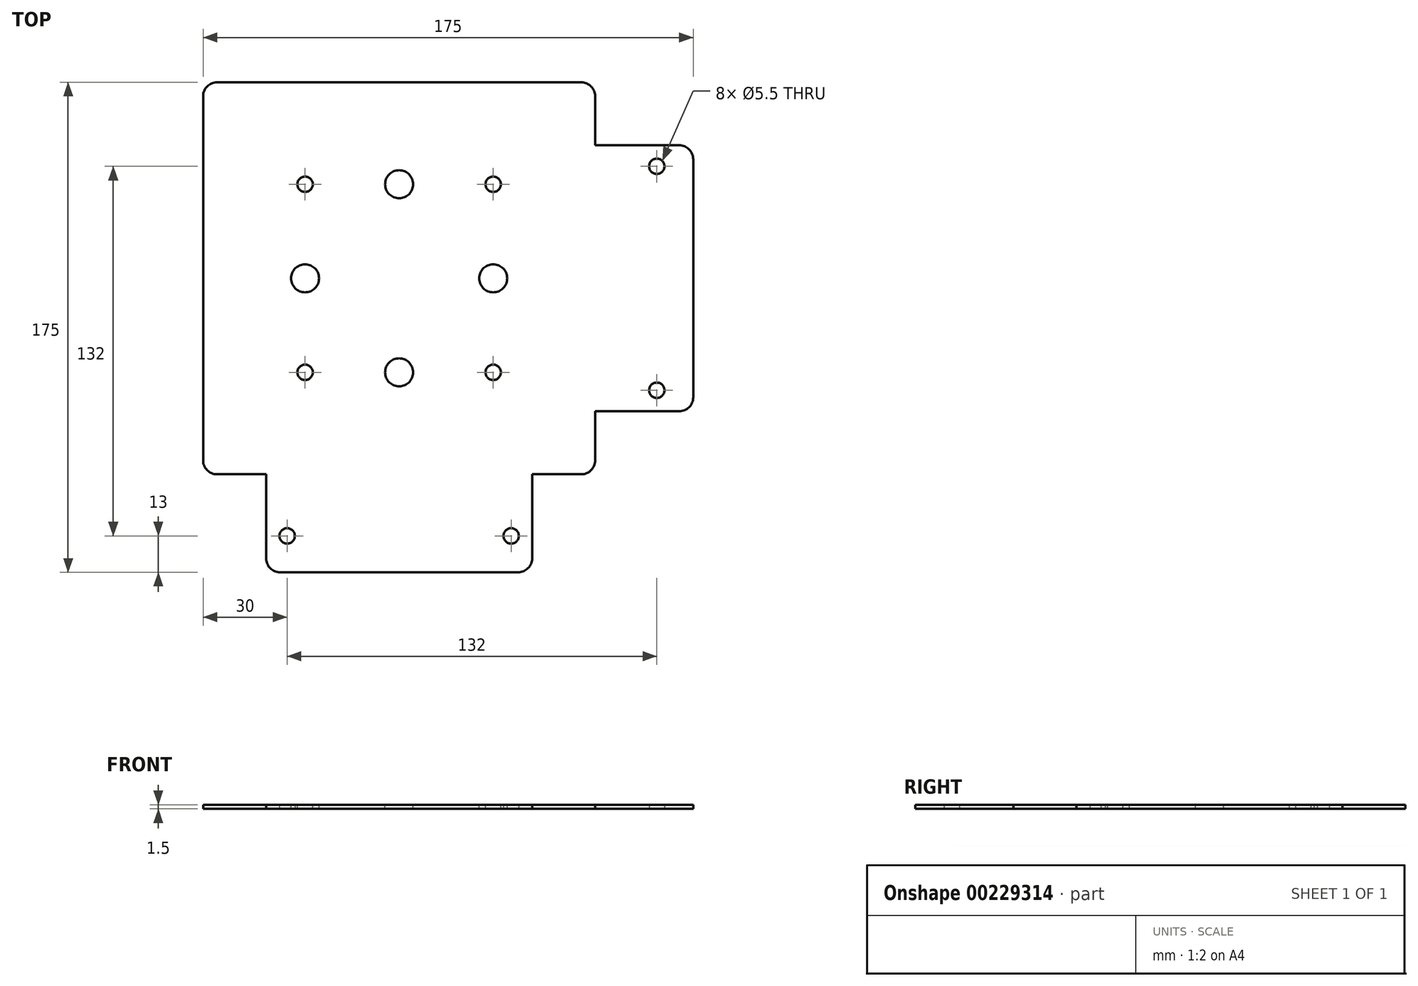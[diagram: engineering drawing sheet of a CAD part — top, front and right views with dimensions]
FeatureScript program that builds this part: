
annotation { "Feature Type Name" : "Feature", "Feature Type Description" : "" }
export const myFeature = defineFeature(function(context is Context, id is Id, definition is map)
    precondition{}
    {
        {
            var Q0;
            Q0=qCreatedBy(makeId("Top.planeOp"),FACE);
            var sketch = newSketch(context, id + "F0", { "sketchPlane" : qUnion([Q0])});
            skLineSegment(sketch, "E0.bottom", {"start": v(-70, 70) * mm, "end": v(70, 70) * mm});
            skLineSegment(sketch, "E0.top", {"start": v(-70, -70) * mm, "end": v(70, -70) * mm});
            skLineSegment(sketch, "E0.left", {"start": v(-70, 70) * mm, "end": v(-70, -70) * mm});
            skLineSegment(sketch, "E0.right", {"start": v(70, 70) * mm, "end": v(70, -70) * mm});
            skPoint(sketch, "E0.middle", {"position": v(0, 0) * mm});
            skLineSegment(sketch, "E1.bottom", {"start": v(-47.5, -70) * mm, "end": v(47.5, -70) * mm});
            skLineSegment(sketch, "E1.top", {"start": v(-47.5, -105) * mm, "end": v(47.5, -105) * mm});
            skLineSegment(sketch, "E1.left", {"start": v(-47.5, -70) * mm, "end": v(-47.5, -105) * mm});
            skLineSegment(sketch, "E1.right", {"start": v(47.5, -70) * mm, "end": v(47.5, -105) * mm});
            skLineSegment(sketch, "E2", {"start": v(70, -70) * mm, "end": v(0, 0) * mm, "construction": true});
            skCircle(sketch, "E3", {"center": v(-40, -92) * mm, "radius": 2.75 * mm});
            skCircle(sketch, "E4", {"center": v(40, -92) * mm, "radius": 2.75 * mm});
            skLineSegment(sketch, "E5.MirrorCS", {"start": v(70, -47.5) * mm, "end": v(105, -47.5) * mm});
            skCircle(sketch, "E6.MirrorC", {"center": v(92, 40) * mm, "radius": 2.75 * mm});
            skCircle(sketch, "E7.MirrorC", {"center": v(92, -40) * mm, "radius": 2.75 * mm});
            skLineSegment(sketch, "E8.MirrorCS", {"start": v(70, 47.5) * mm, "end": v(70, -47.5) * mm});
            skLineSegment(sketch, "E9.MirrorCS", {"start": v(105, 47.5) * mm, "end": v(105, -47.5) * mm});
            skLineSegment(sketch, "E10.MirrorCS", {"start": v(70, 47.5) * mm, "end": v(105, 47.5) * mm});
            skSolve(sketch);
        }
        {
            var Q0;
            Q0 = qSketchRegion(id + "F0", true);
            extrude(context, id + "F1", {"entities" : qUnion([Q0]), "depth" : 1.5 * mm});
        }
        {
            var Q0;
            Q0=makeQuery(id+"F1.opExtrude","CAP_FACE",FACE,{"disambiguationData":[OSD([sQuery(id+"F0.wireOp",EDGE,"E0.bottom"),sQuery(id+"F0.wireOp",EDGE,"E0.top"),sQuery(id+"F0.wireOp",EDGE,"E0.left"),sQuery(id+"F0.wireOp",EDGE,"E0.right")])],"isStart":false});
            var sketch = newSketch(context, id + "F2", { "sketchPlane" : qUnion([Q0])});
            skCircle(sketch, "E11", {"center": v(0, 0) * mm, "radius": 47.5 * mm, "construction": true});
            skCircle(sketch, "E12", {"center": v(-33.59, -33.59) * mm, "radius": 2.75 * mm});
            skLineSegment(sketch, "E13", {"start": v(0, 0) * mm, "end": v(-33.59, -33.59) * mm, "construction": true});
            skCircle(sketch, "E14.MirrorC", {"center": v(33.59, -33.59) * mm, "radius": 2.75 * mm});
            skCircle(sketch, "E15.MirrorC", {"center": v(-33.59, 33.59) * mm, "radius": 2.75 * mm});
            skCircle(sketch, "E16.MirrorC", {"center": v(33.59, 33.59) * mm, "radius": 2.75 * mm});
            skLineSegment(sketch, "E17", {"start": v(-33.59, -33.59) * mm, "end": v(33.59, -33.59) * mm, "construction": true});
            skLineSegment(sketch, "E18", {"start": v(33.59, 33.59) * mm, "end": v(33.59, -33.59) * mm, "construction": true});
            skCircle(sketch, "E19", {"center": v(0, -33.59) * mm, "radius": 5 * mm});
            skCircle(sketch, "E20", {"center": v(33.59, 0) * mm, "radius": 5 * mm});
            skCircle(sketch, "E21.MirrorC", {"center": v(-33.59, 0) * mm, "radius": 5 * mm});
            skCircle(sketch, "E22.MirrorC", {"center": v(0, 33.59) * mm, "radius": 5 * mm});
            skSolve(sketch);
        }
        {
            var Q0;
            Q0 = qSketchRegion(id + "F2", true);
            extrude(context, id + "F3", {"entities" : qUnion([Q0]), "operationType" : NewBodyOperationType.REMOVE, "endBound" : BoundingType.THROUGH_ALL, "oppositeDirection" : true, "depth" : 25 * mm});
        }
        {
            var Q0;
            Q0=makeQuery(id+"F1.opExtrude","SWEPT_EDGE",EDGE,{"disambiguationData":[OSD([sQuery(id+"F0.wireOp",EDGE,"E0.top"),sQuery(id+"F0.wireOp",EDGE,"E0.right")])]});
            var Q1;
            Q1=makeQuery(id+"F1.opExtrude","SWEPT_EDGE",EDGE,{"disambiguationData":[OSD([sQuery(id+"F0.wireOp",EDGE,"E0.top"),sQuery(id+"F0.wireOp",EDGE,"E0.left")])]});
            var Q2;
            Q2=makeQuery(id+"F1.opExtrude","SWEPT_EDGE",EDGE,{"disambiguationData":[OSD([sQuery(id+"F0.wireOp",EDGE,"E0.bottom"),sQuery(id+"F0.wireOp",EDGE,"E0.right")])]});
            var Q3;
            Q3=makeQuery(id+"F1.opExtrude","SWEPT_EDGE",EDGE,{"disambiguationData":[OSD([sQuery(id+"F0.wireOp",EDGE,"E0.bottom"),sQuery(id+"F0.wireOp",EDGE,"E0.left")])]});
            fillet(context, id + "F4", {"entities" : qUnion([Q0, Q1, Q2, Q3]), "radius" : 5 * mm, "tangentPropagation" : true, "allowEdgeOverflow" : false});
        }
        {
            var Q0;
            Q0=makeQuery(id+"F1.opExtrude","SWEPT_EDGE",EDGE,{"disambiguationData":[OSD([sQuery(id+"F0.wireOp",EDGE,"E1.top"),sQuery(id+"F0.wireOp",EDGE,"E1.left")])]});
            var Q1;
            Q1=makeQuery(id+"F1.opExtrude","SWEPT_EDGE",EDGE,{"disambiguationData":[OSD([sQuery(id+"F0.wireOp",EDGE,"E1.top"),sQuery(id+"F0.wireOp",EDGE,"E1.right")])]});
            var Q2;
            Q2=makeQuery(id+"F1.opExtrude","SWEPT_EDGE",EDGE,{"disambiguationData":[OSD([sQuery(id+"F0.wireOp",EDGE,"E5.MirrorCS"),sQuery(id+"F0.wireOp",EDGE,"E9.MirrorCS")])]});
            var Q3;
            Q3=makeQuery(id+"F1.opExtrude","SWEPT_EDGE",EDGE,{"disambiguationData":[OSD([sQuery(id+"F0.wireOp",EDGE,"E9.MirrorCS"),sQuery(id+"F0.wireOp",EDGE,"E10.MirrorCS")])]});
            fillet(context, id + "F5", {"entities" : qUnion([Q0, Q1, Q2, Q3]), "radius" : 5 * mm, "tangentPropagation" : true, "allowEdgeOverflow" : false});
        }
    });
